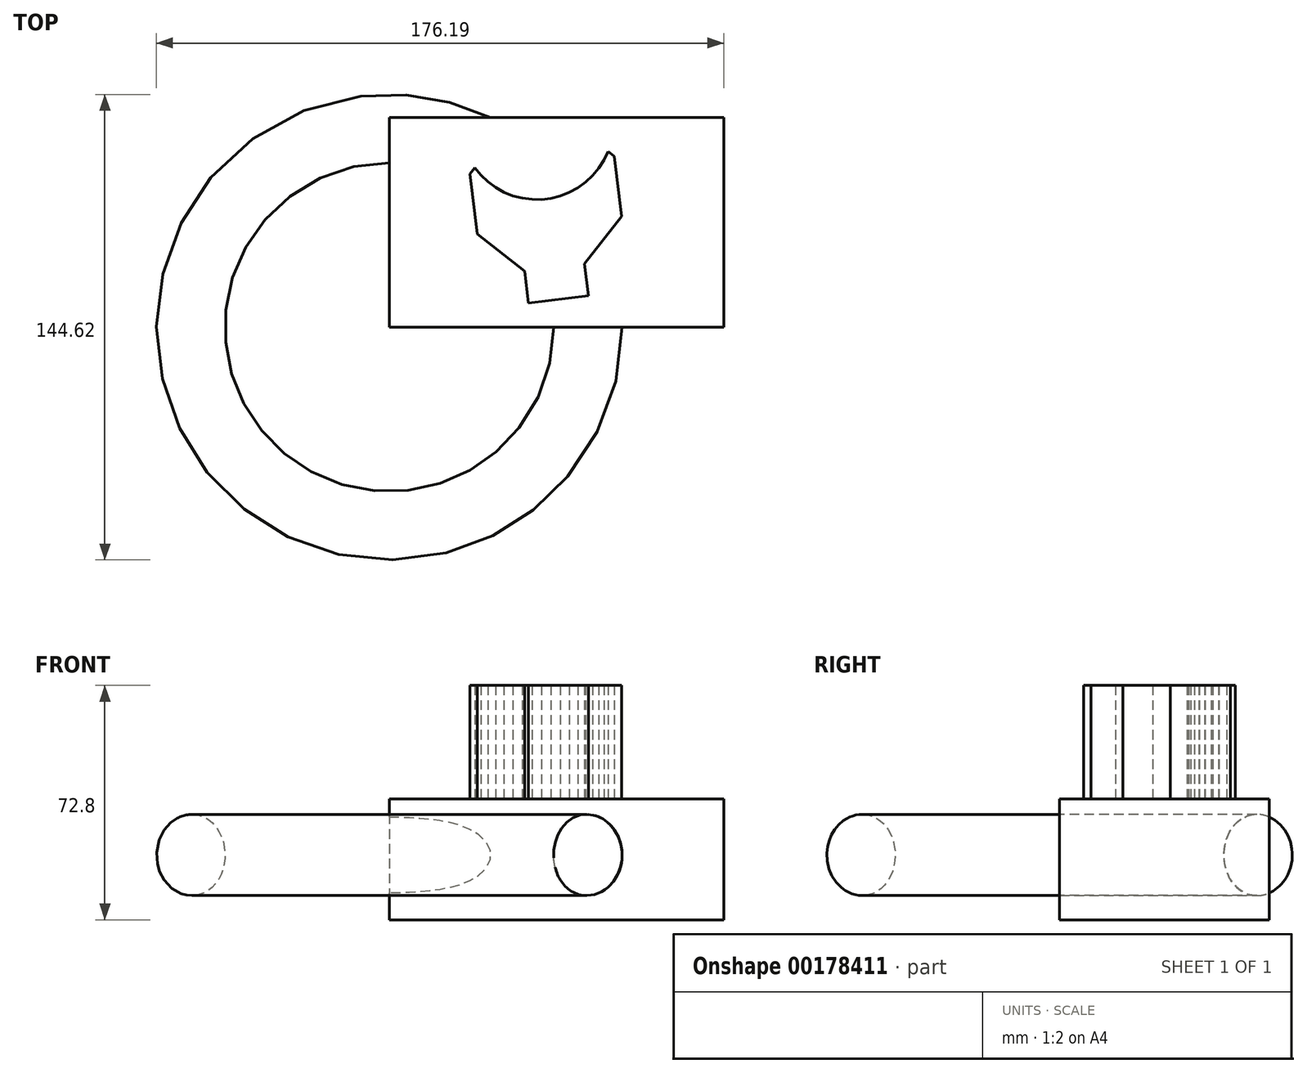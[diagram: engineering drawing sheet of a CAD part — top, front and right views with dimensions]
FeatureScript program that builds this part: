
annotation { "Feature Type Name" : "Feature", "Feature Type Description" : "" }
export const myFeature = defineFeature(function(context is Context, id is Id, definition is map)
    precondition{}
    {
        {
            var Q0;
            Q0=qCreatedBy(makeId("Top.planeOp"),FACE);
            var sketch = newSketch(context, id + "F0", { "sketchPlane" : qUnion([Q0])});
            skLineSegment(sketch, "E0.bottom", {"start": v(51.94, -32.56) * mm, "end": v(-51.94, -32.56) * mm});
            skLineSegment(sketch, "E0.top", {"start": v(51.94, 32.56) * mm, "end": v(-51.94, 32.56) * mm});
            skLineSegment(sketch, "E0.left", {"start": v(51.94, -32.56) * mm, "end": v(51.94, 32.56) * mm});
            skLineSegment(sketch, "E0.right", {"start": v(-51.94, -32.56) * mm, "end": v(-51.94, 32.56) * mm});
            skPoint(sketch, "E0.middle", {"position": v(0, 0) * mm});
            skSolve(sketch);
        }
        {
            var Q0;
            Q0=makeQuery(id+"F0.imprint","IMPRINT",FACE,{"disambiguationData":[TD([[makeQuery(id+"F0.imprint","IMPRINT",EDGE,{"derivedFrom":sQuery(id+"F0.wireOp",EDGE,"E0.bottom")}),-1.0]])]});
            extrude(context, id + "F1", {"entities" : qUnion([Q0]), "depth" : 37.5 * mm});
        }
        {
            var Q0;
            Q0=makeQuery(id+"F1.opExtrude","CAP_FACE",FACE,{"disambiguationData":[OSD([sQuery(id+"F0.wireOp",EDGE,"E0.bottom"),sQuery(id+"F0.wireOp",EDGE,"E0.top"),sQuery(id+"F0.wireOp",EDGE,"E0.left"),sQuery(id+"F0.wireOp",EDGE,"E0.right")])],"isStart":false});
            var sketch = newSketch(context, id + "F2", { "sketchPlane" : qUnion([Q0])});
            skCircle(sketch, "E1.cCircle", {"center": v(-3.34, 8.44) * mm, "radius": 24.5 * mm, "construction": true});
            skLineSegment(sketch, "E1.0", {"start": v(8.72, -12.9) * mm, "end": v(-9.9, -15.17) * mm});
            skLineSegment(sketch, "E1.1", {"start": v(-9.9, -15.17) * mm, "end": v(-24.67, -3.62) * mm});
            skLineSegment(sketch, "E1.2", {"start": v(-24.67, -3.62) * mm, "end": v(-26.95, 15) * mm});
            skLineSegment(sketch, "E1.3", {"start": v(-26.95, 15) * mm, "end": v(-15.4, 29.77) * mm});
            skLineSegment(sketch, "E1.4", {"start": v(-15.4, 29.77) * mm, "end": v(3.22, 32.05) * mm});
            skLineSegment(sketch, "E1.5", {"start": v(3.22, 32.05) * mm, "end": v(18, 20.5) * mm});
            skLineSegment(sketch, "E1.6", {"start": v(18, 20.5) * mm, "end": v(20.27, 1.88) * mm});
            skLineSegment(sketch, "E1.7", {"start": v(20.27, 1.88) * mm, "end": v(8.72, -12.9) * mm});
            skCircle(sketch, "E2.cCircle", {"center": v(-6.09, 30.91) * mm, "radius": 23.84 * mm, "construction": true});
            skLineSegment(sketch, "E2.0", {"start": v(-25.42, 16.96) * mm, "end": v(-27.02, 19.49) * mm});
            skLineSegment(sketch, "E2.1", {"start": v(-27.02, 19.49) * mm, "end": v(-28.29, 22.2) * mm});
            skLineSegment(sketch, "E2.2", {"start": v(-28.29, 22.2) * mm, "end": v(-29.2, 25.05) * mm});
            skLineSegment(sketch, "E2.3", {"start": v(-29.2, 25.05) * mm, "end": v(-29.75, 28) * mm});
            skLineSegment(sketch, "E2.4", {"start": v(-29.75, 28) * mm, "end": v(-29.93, 30.98) * mm});
            skLineSegment(sketch, "E2.5", {"start": v(-29.93, 30.98) * mm, "end": v(-29.74, 33.97) * mm});
            skLineSegment(sketch, "E2.6", {"start": v(-29.74, 33.97) * mm, "end": v(-29.17, 36.91) * mm});
            skLineSegment(sketch, "E2.7", {"start": v(-29.17, 36.91) * mm, "end": v(-28.23, 39.76) * mm});
            skLineSegment(sketch, "E2.8", {"start": v(-28.23, 39.76) * mm, "end": v(-26.95, 42.46) * mm});
            skLineSegment(sketch, "E2.9", {"start": v(-26.95, 42.46) * mm, "end": v(-25.34, 44.99) * mm});
            skLineSegment(sketch, "E2.10", {"start": v(-25.34, 44.99) * mm, "end": v(-23.42, 47.29) * mm});
            skLineSegment(sketch, "E2.11", {"start": v(-23.42, 47.29) * mm, "end": v(-21.23, 49.33) * mm});
            skLineSegment(sketch, "E2.12", {"start": v(-21.23, 49.33) * mm, "end": v(-18.8, 51.08) * mm});
            skLineSegment(sketch, "E2.13", {"start": v(-18.8, 51.08) * mm, "end": v(-16.18, 52.52) * mm});
            skLineSegment(sketch, "E2.14", {"start": v(-16.18, 52.52) * mm, "end": v(-13.39, 53.61) * mm});
            skLineSegment(sketch, "E2.15", {"start": v(-13.39, 53.61) * mm, "end": v(-10.49, 54.35) * mm});
            skLineSegment(sketch, "E2.16", {"start": v(-10.49, 54.35) * mm, "end": v(-7.52, 54.72) * mm});
            skLineSegment(sketch, "E2.17", {"start": v(-7.52, 54.72) * mm, "end": v(-4.52, 54.7) * mm});
            skLineSegment(sketch, "E2.18", {"start": v(-4.52, 54.7) * mm, "end": v(-1.55, 54.32) * mm});
            skLineSegment(sketch, "E2.19", {"start": v(-1.55, 54.32) * mm, "end": v(1.35, 53.57) * mm});
            skLineSegment(sketch, "E2.20", {"start": v(1.35, 53.57) * mm, "end": v(4.13, 52.46) * mm});
            skLineSegment(sketch, "E2.21", {"start": v(4.13, 52.46) * mm, "end": v(6.75, 51) * mm});
            skLineSegment(sketch, "E2.22", {"start": v(6.75, 51) * mm, "end": v(9.17, 49.24) * mm});
            skLineSegment(sketch, "E2.23", {"start": v(9.17, 49.24) * mm, "end": v(11.34, 47.18) * mm});
            skLineSegment(sketch, "E2.24", {"start": v(11.34, 47.18) * mm, "end": v(13.24, 44.87) * mm});
            skLineSegment(sketch, "E2.25", {"start": v(13.24, 44.87) * mm, "end": v(14.84, 42.34) * mm});
            skLineSegment(sketch, "E2.26", {"start": v(14.84, 42.34) * mm, "end": v(16.1, 39.63) * mm});
            skLineSegment(sketch, "E2.27", {"start": v(16.1, 39.63) * mm, "end": v(17.02, 36.77) * mm});
            skLineSegment(sketch, "E2.28", {"start": v(17.02, 36.77) * mm, "end": v(17.58, 33.83) * mm});
            skLineSegment(sketch, "E2.29", {"start": v(17.58, 33.83) * mm, "end": v(17.76, 30.84) * mm});
            skLineSegment(sketch, "E2.30", {"start": v(17.76, 30.84) * mm, "end": v(17.56, 27.85) * mm});
            skLineSegment(sketch, "E2.31", {"start": v(17.56, 27.85) * mm, "end": v(16.99, 24.91) * mm});
            skLineSegment(sketch, "E2.32", {"start": v(16.99, 24.91) * mm, "end": v(16.06, 22.07) * mm});
            skLineSegment(sketch, "E2.33", {"start": v(16.06, 22.07) * mm, "end": v(14.77, 19.36) * mm});
            skLineSegment(sketch, "E2.34", {"start": v(14.77, 19.36) * mm, "end": v(13.16, 16.84) * mm});
            skLineSegment(sketch, "E2.35", {"start": v(13.16, 16.84) * mm, "end": v(11.24, 14.54) * mm});
            skLineSegment(sketch, "E2.36", {"start": v(11.24, 14.54) * mm, "end": v(9.06, 12.5) * mm});
            skLineSegment(sketch, "E2.37", {"start": v(9.06, 12.5) * mm, "end": v(6.63, 10.74) * mm});
            skLineSegment(sketch, "E2.38", {"start": v(6.63, 10.74) * mm, "end": v(4, 9.3) * mm});
            skLineSegment(sketch, "E2.39", {"start": v(4, 9.3) * mm, "end": v(1.21, 8.21) * mm});
            skLineSegment(sketch, "E2.40", {"start": v(1.21, 8.21) * mm, "end": v(-1.7, 7.48) * mm});
            skLineSegment(sketch, "E2.41", {"start": v(-1.7, 7.48) * mm, "end": v(-4.66, 7.11) * mm});
            skLineSegment(sketch, "E2.42", {"start": v(-4.66, 7.11) * mm, "end": v(-7.66, 7.12) * mm});
            skLineSegment(sketch, "E2.43", {"start": v(-7.66, 7.12) * mm, "end": v(-10.63, 7.5) * mm});
            skLineSegment(sketch, "E2.44", {"start": v(-10.63, 7.5) * mm, "end": v(-13.53, 8.26) * mm});
            skLineSegment(sketch, "E2.45", {"start": v(-13.53, 8.26) * mm, "end": v(-16.3, 9.37) * mm});
            skLineSegment(sketch, "E2.46", {"start": v(-16.3, 9.37) * mm, "end": v(-18.93, 10.82) * mm});
            skLineSegment(sketch, "E2.47", {"start": v(-18.93, 10.82) * mm, "end": v(-21.34, 12.59) * mm});
            skLineSegment(sketch, "E2.48", {"start": v(-21.34, 12.59) * mm, "end": v(-23.52, 14.64) * mm});
            skLineSegment(sketch, "E2.49", {"start": v(-23.52, 14.64) * mm, "end": v(-25.42, 16.96) * mm});
            skSolve(sketch);
        }
        {
            var Q0;
            Q0=makeQuery(id+"F2.imprint","IMPRINT",FACE,{"disambiguationData":[TD([[makeQuery(id+"F2.imprint","IMPRINT",EDGE,{"derivedFrom":sQuery(id+"F2.wireOp",EDGE,"E1.0")}),-1.0]])]});
            extrude(context, id + "F3", {"entities" : qUnion([Q0]), "operationType" : NewBodyOperationType.ADD, "depth" : 35.3 * mm});
        }
        {
            var Q0;
            Q0=makeQuery(id+"F3.opExtrude","SWEPT_FACE",FACE,{"disambiguationData":[OSD([sQuery(id+"F2.wireOp",EDGE,"E1.0")])]});
            extrude(context, id + "F4", {"entities" : qUnion([Q0]), "operationType" : NewBodyOperationType.ADD, "depth" : 10 * mm});
        }
        {
            var Q0;
            Q0=qCreatedBy(makeId("Front.planeOp"),FACE);
            var sketch = newSketch(context, id + "F5", { "sketchPlane" : qUnion([Q0])});
            skCircle(sketch, "E3", {"center": v(0, 20.13) * mm, "radius": 12.62 * mm});
            skSolve(sketch);
        }
        {
            var Q0;
            Q0 = qSketchRegion(id + "F5", true);
            var Q1;
            Q1=makeQuery(id+"F1.opExtrude","SWEPT_EDGE",EDGE,{"disambiguationData":[OSD([sQuery(id+"F0.wireOp",EDGE,"E0.bottom"),sQuery(id+"F0.wireOp",EDGE,"E0.right")])]});
            revolve(context, id + "F6", {"operationType" : NewBodyOperationType.ADD, "entities" : qUnion([Q0]), "axis" : qUnion([Q1]), "revolveType" : RevolveType.FULL});
        }
        {
            var Q0;
            Q0=makeQuery(id+"F1.opExtrude","CAP_FACE",FACE,{"disambiguationData":[OSD([sQuery(id+"F0.wireOp",EDGE,"E0.bottom"),sQuery(id+"F0.wireOp",EDGE,"E0.top"),sQuery(id+"F0.wireOp",EDGE,"E0.left"),sQuery(id+"F0.wireOp",EDGE,"E0.right")])],"isStart":true});
            var sketch = newSketch(context, id + "F7", { "sketchPlane" : qUnion([Q0])});
            skCircle(sketch, "E4.cCircle", {"center": v(0, 0) * mm, "radius": 16.07 * mm, "construction": true});
            skLineSegment(sketch, "E4.0", {"start": v(27.92, 15.92) * mm, "end": v(-0.17, -32.14) * mm});
            skLineSegment(sketch, "E4.1", {"start": v(-0.17, -32.14) * mm, "end": v(-27.75, 16.21) * mm});
            skLineSegment(sketch, "E4.2", {"start": v(-27.75, 16.21) * mm, "end": v(27.92, 15.92) * mm});
            skPoint(sketch, "E4.0.midPoint", {"position": v(13.87, -8.1) * mm});
            skSolve(sketch);
        }
        {
            var Q0;
            Q0=makeQuery(id+"F7.imprint","IMPRINT",FACE,{"disambiguationData":[TD([[makeQuery(id+"F7.imprint","IMPRINT",EDGE,{"derivedFrom":sQuery(id+"F7.wireOp",EDGE,"E4.0")}),-1.0]])]});
            extrude(context, id + "F8", {"entities" : qUnion([Q0]), "operationType" : NewBodyOperationType.ADD, "oppositeDirection" : true, "depth" : 25 * mm});
        }
        {
            var Q0;
            Q0=makeQuery(id+"F1.opExtrude","SWEPT_FACE",FACE,{"disambiguationData":[OSD([sQuery(id+"F0.wireOp",EDGE,"E0.left")])]});
            var sketch = newSketch(context, id + "F9", { "sketchPlane" : qUnion([Q0])});
            skCircle(sketch, "E5", {"center": v(0, 19.44) * mm, "radius": 16 * mm});
            skSolve(sketch);
        }
        {
            var Q0;
            Q0 = qSketchRegion(id + "F9", true);
            extrude(context, id + "F10", {"entities" : qUnion([Q0]), "operationType" : NewBodyOperationType.ADD, "oppositeDirection" : true, "depth" : 50 * mm});
        }
    });
